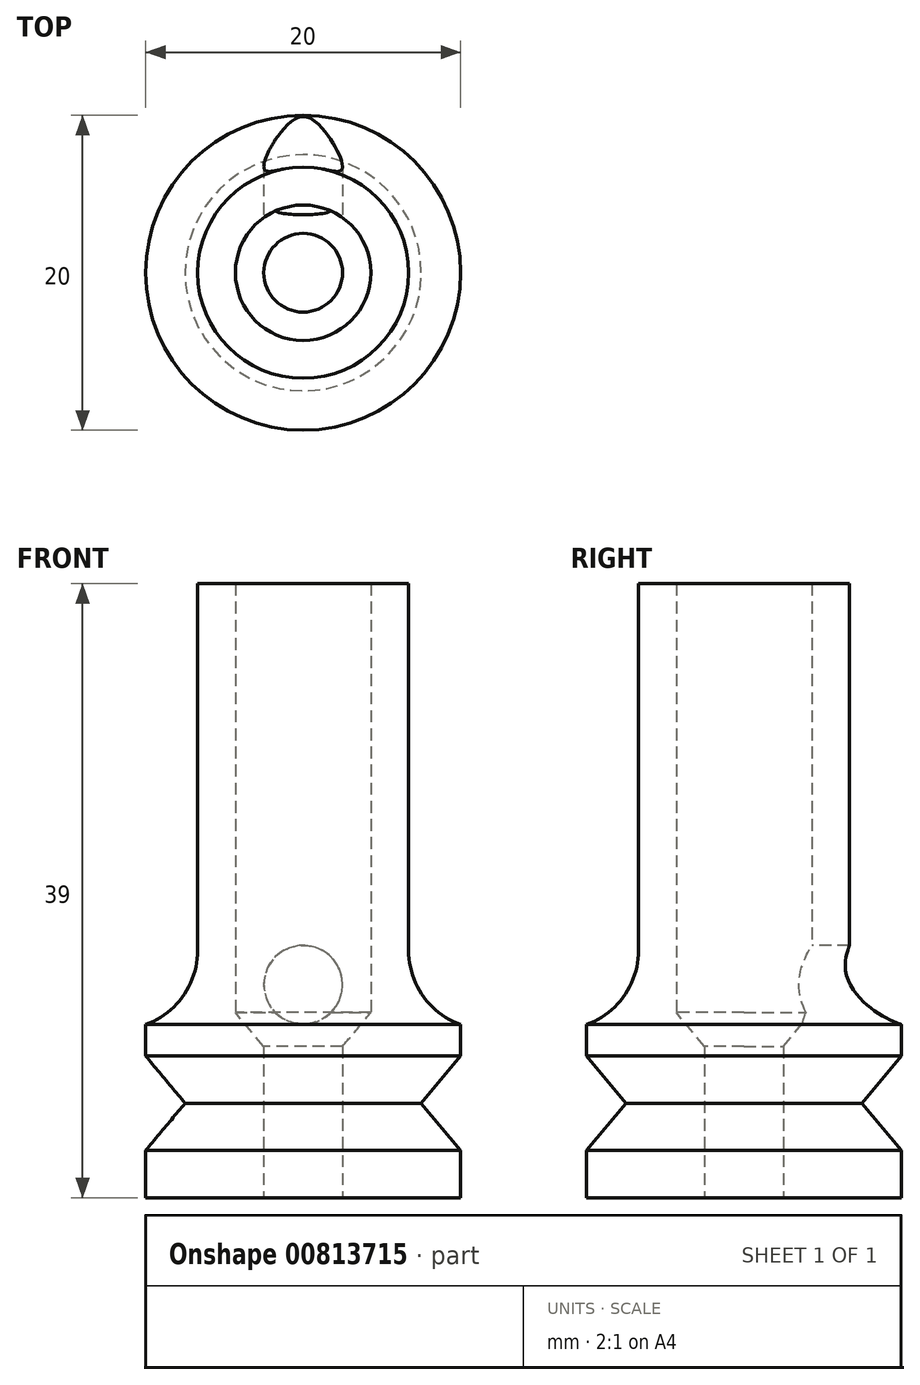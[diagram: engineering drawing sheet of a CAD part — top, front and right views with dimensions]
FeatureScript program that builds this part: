
annotation { "Feature Type Name" : "Feature", "Feature Type Description" : "" }
export const myFeature = defineFeature(function(context is Context, id is Id, definition is map)
    precondition{}
    {
        {
            var Q0;
            Q0=qCreatedBy(makeId("Front.planeOp"),FACE);
            var sketch = newSketch(context, id + "F0", { "sketchPlane" : qUnion([Q0])});
            skLineSegment(sketch, "E0", {"start": v(-2, 0) * mm, "end": v(-10, 0) * mm});
            skLineSegment(sketch, "E1", {"start": v(-10, 0) * mm, "end": v(-10, 3) * mm});
            skLineSegment(sketch, "E2", {"start": v(-10, 3) * mm, "end": v(-7.5, 6) * mm});
            skLineSegment(sketch, "E3", {"start": v(-7.5, 6) * mm, "end": v(-10, 9) * mm});
            skLineSegment(sketch, "E4", {"start": v(-10, 9) * mm, "end": v(-10, 11) * mm});
            skLineSegment(sketch, "E5", {"start": v(-6.7, 11) * mm, "end": v(-10, 11) * mm});
            skLineSegment(sketch, "E6", {"start": v(-6.7, 11) * mm, "end": v(-6.7, 39) * mm});
            skLineSegment(sketch, "E7", {"start": v(-6.7, 39) * mm, "end": v(-4.3, 39) * mm});
            skLineSegment(sketch, "E8", {"start": v(-4.3, 39) * mm, "end": v(-4.3, 11.76) * mm});
            skLineSegment(sketch, "E9", {"start": v(0, -5.68) * mm, "end": v(0, 50.8) * mm, "construction": true});
            skLineSegment(sketch, "E10", {"start": v(-2, 0) * mm, "end": v(-2, 9) * mm});
            skLineSegment(sketch, "E11", {"start": v(-2, 9) * mm, "end": v(-4.3, 11.76) * mm});
            skSolve(sketch);
        }
        {
            var Q0;
            {var subQ0=sQuery(id+"F0.wireOp",EDGE,"E6");Q0=makeQuery(id+"F0.imprint","IMPRINT",FACE,{"disambiguationData":[TD([[makeQuery(id+"F0.imprint","IMPRINT",EDGE,{"derivedFrom":subQ0}),-1.0]])]});}
            var Q1;
            Q1=makeQuery(id+"F0.imprint","IMPRINT",FACE,{"disambiguationData":[TD([[makeQuery(id+"F0.imprint","IMPRINT",EDGE,{"derivedFrom":sQuery(id+"F0.wireOp",EDGE,"E0")}),-1.0]])]});
            var Q2;
            {var subQ3=sQuery(id+"F0.wireOp",EDGE,"TWkmGITD-2UAL-noeB-LUlV-Z9KWvzIweCRO");Q2=makeQuery(id+"F0.imprint","IMPRINT",FACE,{"disambiguationData":[TD([[makeQuery(id+"F0.imprint","IMPRINT",EDGE,{"derivedFrom":subQ3}),1.0]])]});}
            var Q3;
            Q3=sQuery(id+"F0.wireOp",EDGE,"E9");
            revolve(context, id + "F1", {"surfaceOperationType" : NewSurfaceOperationType.NEW, "entities" : qUnion([Q0, Q1, Q2]), "axis" : qUnion([Q3]), "revolveType" : RevolveType.FULL});
        }
        {
            var Q0;
            Q0=makeQuery(id+"F1.opRevolve","SWEPT_EDGE",EDGE,{"disambiguationData":[OSD([sQuery(id+"F0.wireOp",EDGE,"E5"),sQuery(id+"F0.wireOp",EDGE,"E6")])]});
            fillet(context, id + "F2", {"entities" : qUnion([Q0]), "radius" : 5 * mm, "tangentPropagation" : true, "allowEdgeOverflow" : false});
        }
        {
            var Q0;
            Q0=makeQuery(id+"F1.opRevolve","SWEPT_FACE",FACE,{"disambiguationData":[OSD([sQuery(id+"F0.wireOp",EDGE,"E0")])]});
            var sketch = newSketch(context, id + "F3", { "sketchPlane" : qUnion([Q0])});
            skCircle(sketch, "E12", {"center": v(0, 0) * mm, "radius": 2.5 * mm});
            skSolve(sketch);
        }
        {
            var Q0;
            Q0=makeQuery(id+"F3.imprint","IMPRINT",FACE,{"disambiguationData":[TD([[makeQuery(id+"F3.imprint","IMPRINT",EDGE,{"derivedFrom":sQuery(id+"F3.wireOp",EDGE,"E12")}),1.0]])]});
            extrude(context, id + "F4", {"entities" : qUnion([Q0]), "operationType" : NewBodyOperationType.REMOVE, "oppositeDirection" : true, "depth" : 25 * mm, "offsetDistance" : 25 * mm});
        }
        {
            var Q0;
            Q0=qCreatedBy(makeId("Front.planeOp"),FACE);
            var sketch = newSketch(context, id + "F5", { "sketchPlane" : qUnion([Q0])});
            skCircle(sketch, "E13", {"center": v(0, 13.53) * mm, "radius": 2.5 * mm});
            skSolve(sketch);
        }
        {
            var Q0;
            Q0=makeQuery(id+"F5.imprint","IMPRINT",FACE,{"disambiguationData":[TD([[makeQuery(id+"F5.imprint","IMPRINT",EDGE,{"derivedFrom":sQuery(id+"F5.wireOp",EDGE,"E13")}),1.0]])]});
            extrude(context, id + "F6", {"entities" : qUnion([Q0]), "operationType" : NewBodyOperationType.REMOVE, "oppositeDirection" : true, "depth" : 25 * mm, "offsetDistance" : 25 * mm});
        }
    });
